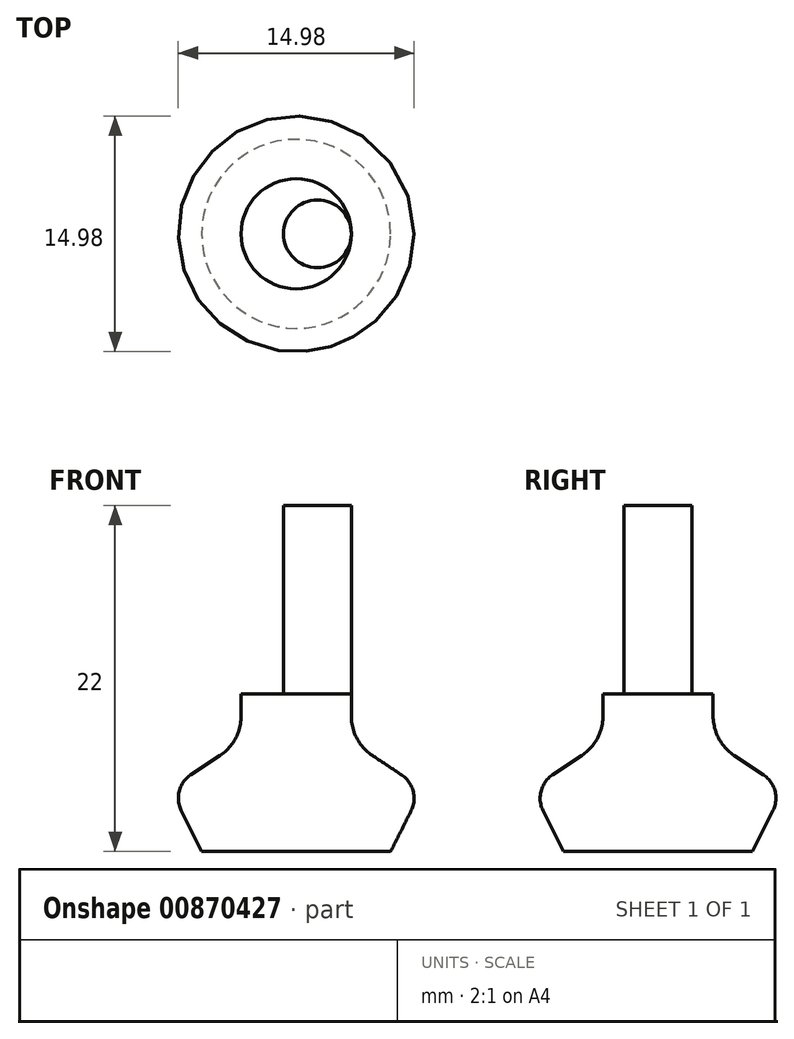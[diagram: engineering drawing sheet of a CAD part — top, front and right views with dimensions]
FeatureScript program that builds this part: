
annotation { "Feature Type Name" : "Feature", "Feature Type Description" : "" }
export const myFeature = defineFeature(function(context is Context, id is Id, definition is map)
    precondition{}
    {
        {
            var Q0;
            Q0=qCreatedBy(makeId("Front.planeOp"),FACE);
            var sketch = newSketch(context, id + "F0", { "sketchPlane" : qUnion([Q0])});
            skLineSegment(sketch, "E0", {"start": v(0, 0) * mm, "end": v(-6, 0) * mm});
            skLineSegment(sketch, "E1", {"start": v(-6, 0) * mm, "end": v(-8, 4) * mm});
            skLineSegment(sketch, "E2", {"start": v(-8, 4) * mm, "end": v(-4.84, 6.1) * mm});
            skLineSegment(sketch, "E3", {"start": v(-3.5, 8.6) * mm, "end": v(-3.5, 10) * mm});
            skLineSegment(sketch, "E4", {"start": v(0, 10) * mm, "end": v(0, 0) * mm});
            skLineSegment(sketch, "E5", {"start": v(-3.5, 10) * mm, "end": v(0, 10) * mm});
            skPoint(sketch, "E6.visualSharp", {"position": v(-3.5, 7) * mm});
            skArc(sketch, "E6.filletArc", {"start": v(-4.84, 6.1) * mm, "mid": v(-3.85, 7.19) * mm, "end": v(-3.5, 8.6) * mm});
            skSolve(sketch);
        }
        {
            var Q0;
            Q0 = qSketchRegion(id + "F0", true);
            var Q1;
            Q1=sQuery(id+"F0.wireOp",EDGE,"E4");
            revolve(context, id + "F1", {"surfaceOperationType" : NewSurfaceOperationType.NEW, "entities" : qUnion([Q0]), "axis" : qUnion([Q1]), "revolveType" : RevolveType.FULL});
        }
        {
            var Q0;
            Q0=makeQuery(id+"F1.opRevolve","SWEPT_EDGE",EDGE,{"disambiguationData":[OSD([sQuery(id+"F0.wireOp",EDGE,"E1"),sQuery(id+"F0.wireOp",EDGE,"E2")])]});
            fillet(context, id + "F2", {"entities" : qUnion([Q0]), "radius" : 1.77 * mm, "tangentPropagation" : true, "allowEdgeOverflow" : false});
        }
        {
            var Q0;
            Q0=makeQuery(id+"F1.opRevolve","SWEPT_FACE",FACE,{"disambiguationData":[OSD([sQuery(id+"F0.wireOp",EDGE,"E5")])]});
            var sketch = newSketch(context, id + "F3", { "sketchPlane" : qUnion([Q0])});
            skCircle(sketch, "E7", {"center": v(1.35, 0) * mm, "radius": 2.15 * mm});
            skSolve(sketch);
        }
        {
            var Q0;
            Q0 = qSketchRegion(id + "F3", true);
            extrude(context, id + "F4", {"entities" : qUnion([Q0]), "operationType" : NewBodyOperationType.ADD, "depth" : 12 * mm, "offsetDistance" : 25 * mm});
        }
    });
